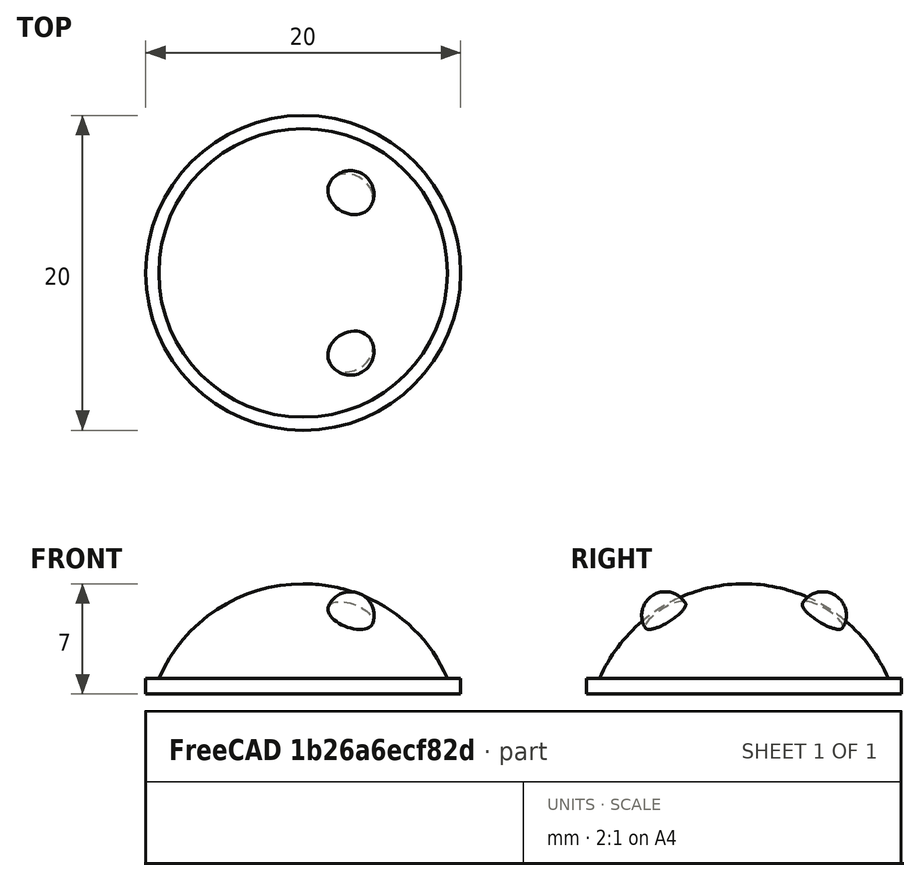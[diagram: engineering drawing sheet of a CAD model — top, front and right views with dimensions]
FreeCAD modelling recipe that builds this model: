
FCSTD DOCUMENT  (FreeCAD 0.18.4R)
Label: tutorial_freecad_ex13_b
License: All rights reserved
LicenseURL: http://en.wikipedia.org/wiki/All_rights_reserved
objects: Part::Sphere×3, Part::MultiFuse×3, Part::Cylinder×1
note: 7 computed .brp shape members not serialized (recipe doc carries the construction recipe); baked Part::Feature solids carry a one-line shape summary decoded from their .brp

FEATURE [Part::Sphere] Sphere  label="cabeza"
  Angle1 = 20
  Angle2 = 90
  Angle3 = 360
  AttacherType = Attacher::AttachEngine3D
  Placement = pos=(0,0,-3) rot=(0,0,1;0rad)
  Radius = 10
FEATURE [Part::Cylinder] Cylinder  label="Cilindro"
  Angle = 360
  AttacherType = Attacher::AttachEngine3D
  Height = 1
  Radius = 10
FEATURE [Part::MultiFuse] Fusion
  Refine = true
  Shapes = -> [Sphere,Cylinder]
FEATURE [Part::Sphere] Sphere001  label="Esfera"
  Angle1 = -90
  Angle2 = 90
  Angle3 = 360
  AttacherType = Attacher::AttachEngine3D
  Placement = pos=(3,5,5) rot=(0,0,1;0rad)
  Radius = 1.5
FEATURE [Part::Sphere] Sphere002  label="Esfera001"
  Angle1 = -90
  Angle2 = 90
  Angle3 = 360
  AttacherType = Attacher::AttachEngine3D
  Placement = pos=(3,-5,5) rot=(0,0,1;0rad)
  Radius = 1.5
FEATURE [Part::MultiFuse] Fusion001
  Refine = true
  Shapes = -> [Sphere001,Sphere002]
FEATURE [Part::MultiFuse] Fusion002
  Refine = true
  Shapes = -> [Fusion,Fusion001]
